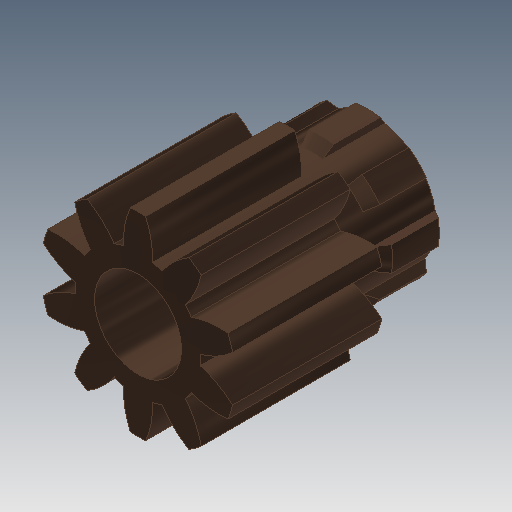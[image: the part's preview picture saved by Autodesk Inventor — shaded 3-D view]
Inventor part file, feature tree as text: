
AUTODESK INVENTOR PART (.ipt)
format: ipt  version: 2017 (Build 210142000, 142)  size: 270,336 bytes
history: native  units: mm (DEFAULTED — no unit token found)
features: sketch x5, extrude x4, plane x3, other x3, chamfer x2, pattern_circular x1, projected_geometry x1
ambient origin geometry x8: Origin, YZ Plane, XZ Plane, XY Plane, X Axis, Y Axis, Z Axis, Center Point
bodies: Solid1 (feature_tree)
feature tree (19):
  extrude  "Extrusion1"  Depth=2.4mm TaperAngle=0.0deg
  plane  "Work Plane2"
  plane  "Work Plane8"
  plane  "Work Plane9"
  other  "Цилиндрическое зубчатое зацепление"
  extrude  "Выдавливание2"  Depth=10.0mm TaperAngle=0.0deg
  extrude  "Выдавливание3"  Depth=1.4mm
  chamfer  "Фаска1"  Distance=3.141593mm
  chamfer  "Фаска2"  [1 undecoded]
  pattern_circular  "Круговой массив1"  [2 undecoded]
  extrude  "Выдавливание4"  Depth=1.4mm
  sketch  "Sketch1"  dims[d0=3.135mm d1=2.4mm d2=0.0mm]
  sketch  "Sketch2"  dims[d3=2.5mm d4=10.0mm d5=0.0mm d16=6.0mm d17=0.0mm d34=3.141593mm d39=0.0mm d41=0.0mm d43=6.0mm d46=6.0mm d47=0.0mm d48=0.0mm d49=2.0mm d50=1.4mm d51=0.0mm d52=0.15mm d53=3.490659mm d54=1.0mm d55=0.0mm d56=0.15mm d57=2.0mm d58=45.0deg d59=0.15mm d60=0.1mm d61=45.0deg d62=80.0mm d63=360.0deg d65=1.4mm d66=8.0mm d67=0.0mm]
  other  "Srf1"
  sketch  "Эскиз3"
  sketch  "Эскиз4"
  projected_geometry  "Спроецированная петля1"
  sketch  "Эскиз5"
  other  "Средний диаметр"
note: 3 required parameter values undecoded (feature->parameter linkage not recoverable at this tier; creation-order binding heuristic only, values carry confidence <= 0.55)
